# Revit family: PRD_FrankeWS_ShwrHds_ShowerHead_SHAC0008
name_source: partatom
category: Plumbing Fixtures
revit_build: Autodesk Revit 2018 (Build: 20190510_1515(x64)
units: mm (PartAtom-declared; Revit-internal decimal feet)

## family parameters
Cut with Voids When Loaded = No
Host = Face
OmniClass Number = 23.45.55.14
OmniClass Title = Single Faucets
Part Type = Normal
Room Calculation Point = No
Round Connector Dimension = Use Diameter
Shared = No

## types (1)
- SHAC0008
    AssetType = Fixed
    BIMObjectName = PRD_AR_ShowerHeads_ShowerHead_SHAC0008
    Category = Pr_40_20_87_76, Shower heads
    Color = Chrome
    Default Elevation = 2100 mm
    Description = AQUAJET-Comfort shower head DN 15 with infinitely angle-adjustable plastic jet face 13° - 23°, anti-calcification system and low aerosol formation.Model for surface pipe installation 18 mm and enclosed flow controllers 0.10 l/s, 0.15 l/s and 0.20 l/s.Housing polished chromium-plated brass. Also suitable for shower trays, 800 x 800 mm.
    DrainSize = 0 mm  [stored 0 ft]
    DurationUnit = year
    Finish = Chrome
    GrossWeight = 1.20 kg
    HasTray = No
    IfcExportAs = IfcSanitaryTerminalType
    IfcExportType = SHOWER
    Manufacturer = KWC Group AG
    ManufacturerName = KWC Group AG
    ManufacturerURL = www.kwc.com
    MaterialThickness = 0 mm  [stored 0 ft]
    Model = SHAC0008
    ModelNumber = 2030021283
    ModelReference = SHAC0008
    NBSDescription = Shower heads
    NBSReference = 45-35-70/333
    Name = Shower head SHAC0008
    NetWeight = 1.14 kg
    NominalDepth = 140 mm  [stored 0.459318 ft]
    NominalHeight = 73 mm  [stored 0.239501 ft]
    NominalLength = 94 mm  [stored 0.308399 ft]
    NominalWidth = 73 mm  [stored 0.239501 ft]
    ProductInformation = https://pim.kwc.com
    ShowerHeadMaterial = PRD_AR_ChromatedBrass_HighPolished
    ShowerType = Other
    Size = 140 x 94 x 73 mm
    URL = www.kwc.com
    Uniclass2015Code = Pr_40_20_87_76
    Uniclass2015Title = Shower heads
    Uniclass2015Version = Products v1.7
    Version = 1
    WarrantyDurationUnit = year

note: [stored X ft] marks values corroborated as IEEE doubles in the binary element streams (Revit-internal decimal feet)

## geometry (parser evidence)
native form markers: Sweep x2
no freeform markers — native parametric forms only
